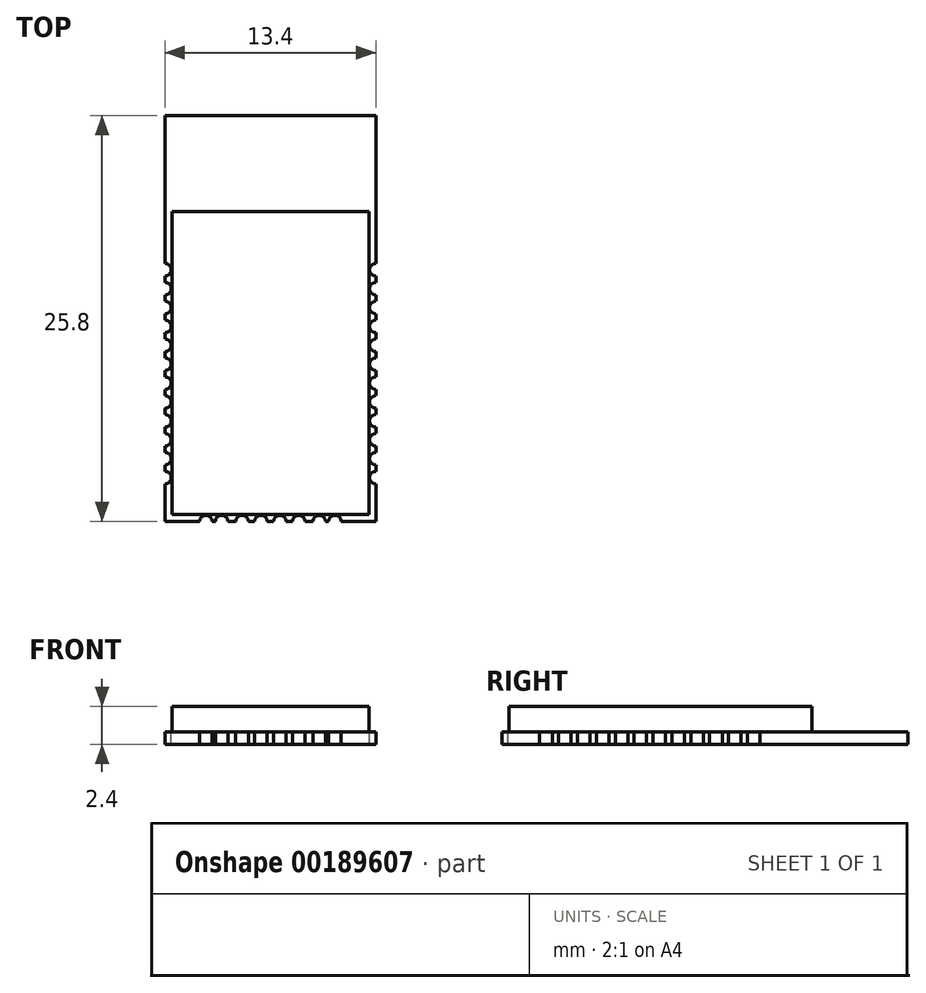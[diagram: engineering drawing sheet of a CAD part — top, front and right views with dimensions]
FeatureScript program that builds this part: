
annotation { "Feature Type Name" : "Feature", "Feature Type Description" : "" }
export const myFeature = defineFeature(function(context is Context, id is Id, definition is map)
    precondition{}
    {
        {
            var Q0;
            Q0=qCreatedBy(makeId("Top.planeOp"),FACE);
            var sketch = newSketch(context, id + "F0", { "sketchPlane" : qUnion([Q0])});
            skLineSegment(sketch, "E0.bottom", {"start": v(-6.7, 0) * mm, "end": v(6.7, 0) * mm});
            skLineSegment(sketch, "E0.top", {"start": v(-6.7, 25.8) * mm, "end": v(6.7, 25.8) * mm});
            skLineSegment(sketch, "E0.left", {"start": v(-6.7, 0) * mm, "end": v(-6.7, 25.8) * mm});
            skLineSegment(sketch, "E0.right", {"start": v(6.7, 0) * mm, "end": v(6.7, 25.8) * mm});
            skPoint(sketch, "E1", {"position": v(0, 0) * mm});
            skSolve(sketch);
        }
        {
            var Q0;
            Q0=qSketchRegion(id+"F0",true);
            extrude(context, id + "F1", {"entities" : qUnion([Q0]), "depth" : 0.8 * mm});
        }
        {
            var Q0;
            Q0=makeQuery(id+"F1.opExtrude","CAP_FACE",FACE,{"disambiguationData":[OSD([sQuery(id+"F0.wireOp",EDGE,"E0.bottom"),sQuery(id+"F0.wireOp",EDGE,"E0.top"),sQuery(id+"F0.wireOp",EDGE,"E0.left"),sQuery(id+"F0.wireOp",EDGE,"E0.right")])],"isStart":false});
            var sketch = newSketch(context, id + "F2", { "sketchPlane" : qUnion([Q0])});
            skCircle(sketch, "E2", {"center": v(-6.7, 2.8) * mm, "radius": 0.4 * mm});
            skLineSegment(sketch, "E3", {"start": v(0, 14.34) * mm, "end": v(0, 6.42) * mm});
            skCircle(sketch, "E4.0.1.0", {"center": v(-6.7, 4) * mm, "radius": 0.4 * mm});
            skCircle(sketch, "E4.0.2.0", {"center": v(-6.7, 5.2) * mm, "radius": 0.4 * mm});
            skCircle(sketch, "E4.0.3.0", {"center": v(-6.7, 6.4) * mm, "radius": 0.4 * mm});
            skCircle(sketch, "E4.0.4.0", {"center": v(-6.7, 7.6) * mm, "radius": 0.4 * mm});
            skCircle(sketch, "E4.0.5.0", {"center": v(-6.7, 8.8) * mm, "radius": 0.4 * mm});
            skCircle(sketch, "E4.0.6.0", {"center": v(-6.7, 10) * mm, "radius": 0.4 * mm});
            skCircle(sketch, "E4.0.7.0", {"center": v(-6.7, 11.2) * mm, "radius": 0.4 * mm});
            skCircle(sketch, "E4.0.8.0", {"center": v(-6.7, 12.4) * mm, "radius": 0.4 * mm});
            skCircle(sketch, "E4.0.9.0", {"center": v(-6.7, 13.6) * mm, "radius": 0.4 * mm});
            skCircle(sketch, "E4.0.10.0", {"center": v(-6.7, 14.8) * mm, "radius": 0.4 * mm});
            skCircle(sketch, "E4.0.11.0", {"center": v(-6.7, 16) * mm, "radius": 0.4 * mm});
            skCircle(sketch, "E4.1.0.0", {"center": v(6.7, 2.8) * mm, "radius": 0.4 * mm});
            skCircle(sketch, "E4.1.1.0", {"center": v(6.7, 4) * mm, "radius": 0.4 * mm});
            skCircle(sketch, "E4.1.2.0", {"center": v(6.7, 5.2) * mm, "radius": 0.4 * mm});
            skCircle(sketch, "E4.1.3.0", {"center": v(6.7, 6.4) * mm, "radius": 0.4 * mm});
            skCircle(sketch, "E4.1.4.0", {"center": v(6.7, 7.6) * mm, "radius": 0.4 * mm});
            skCircle(sketch, "E4.1.5.0", {"center": v(6.7, 8.8) * mm, "radius": 0.4 * mm});
            skCircle(sketch, "E4.1.6.0", {"center": v(6.7, 10) * mm, "radius": 0.4 * mm});
            skCircle(sketch, "E4.1.7.0", {"center": v(6.7, 11.2) * mm, "radius": 0.4 * mm});
            skCircle(sketch, "E4.1.8.0", {"center": v(6.7, 12.4) * mm, "radius": 0.4 * mm});
            skCircle(sketch, "E4.1.9.0", {"center": v(6.7, 13.6) * mm, "radius": 0.4 * mm});
            skCircle(sketch, "E4.1.10.0", {"center": v(6.7, 14.8) * mm, "radius": 0.4 * mm});
            skCircle(sketch, "E4.1.11.0", {"center": v(6.7, 16) * mm, "radius": 0.4 * mm});
            skLineSegment(sketch, "E4.direction1", {"start": v(-6.7, 2.8) * mm, "end": v(6.7, 2.8) * mm, "construction": true});
            skLineSegment(sketch, "E4.direction2", {"start": v(-6.7, 2.8) * mm, "end": v(-6.7, 4) * mm, "construction": true});
            skCircle(sketch, "E5", {"center": v(-4.1, 0) * mm, "radius": 0.4 * mm});
            skCircle(sketch, "E6.1.0.0", {"center": v(-3.1, 0) * mm, "radius": 0.4 * mm});
            skLineSegment(sketch, "E6.direction1", {"start": v(-4.1, 0) * mm, "end": v(-3.1, 0) * mm, "construction": true});
            skCircle(sketch, "E7", {"center": v(-1.8, 0) * mm, "radius": 0.4 * mm});
            skCircle(sketch, "E8.1.0.0", {"center": v(-0.6, 0) * mm, "radius": 0.4 * mm});
            skCircle(sketch, "E8.2.0.0", {"center": v(0.6, 0) * mm, "radius": 0.4 * mm});
            skCircle(sketch, "E8.3.0.0", {"center": v(1.8, 0) * mm, "radius": 0.4 * mm});
            skLineSegment(sketch, "E8.direction1", {"start": v(-1.8, 0) * mm, "end": v(-0.6, 0) * mm, "construction": true});
            skCircle(sketch, "E9", {"center": v(3.1, 0) * mm, "radius": 0.4 * mm});
            skCircle(sketch, "E10.1.0.0", {"center": v(4.1, 0) * mm, "radius": 0.4 * mm});
            skLineSegment(sketch, "E10.direction1", {"start": v(3.1, 0) * mm, "end": v(4.1, 0) * mm, "construction": true});
            skSolve(sketch);
        }
        {
            var Q0;
            Q0=qSketchRegion(id+"F2",true);
            extrude(context, id + "F3", {"entities" : qUnion([Q0]), "operationType" : NewBodyOperationType.REMOVE, "oppositeDirection" : true, "depth" : 25 * mm});
        }
        {
            var Q0;
            Q0=makeQuery(id+"F1.opExtrude","CAP_FACE",FACE,{"disambiguationData":[OSD([sQuery(id+"F0.wireOp",EDGE,"E0.bottom"),sQuery(id+"F0.wireOp",EDGE,"E0.top"),sQuery(id+"F0.wireOp",EDGE,"E0.left"),sQuery(id+"F0.wireOp",EDGE,"E0.right")])],"isStart":false});
            var sketch = newSketch(context, id + "F4", { "sketchPlane" : qUnion([Q0])});
            skLineSegment(sketch, "E11.bottom", {"start": v(-6.26, 0.45) * mm, "end": v(6.26, 0.45) * mm});
            skLineSegment(sketch, "E11.top", {"start": v(-6.26, 19.7) * mm, "end": v(6.26, 19.7) * mm});
            skLineSegment(sketch, "E11.left", {"start": v(-6.26, 0.45) * mm, "end": v(-6.26, 19.7) * mm});
            skLineSegment(sketch, "E11.right", {"start": v(6.26, 0.45) * mm, "end": v(6.26, 19.7) * mm});
            skPoint(sketch, "E12", {"position": v(0, 0.45) * mm});
            skSolve(sketch);
        }
        {
            var Q0;
            Q0=qSketchRegion(id+"F4",true);
            extrude(context, id + "F5", {"entities" : qUnion([Q0]), "operationType" : NewBodyOperationType.ADD, "depth" : (2.4 - 0.8) * mm});
        }
    });
